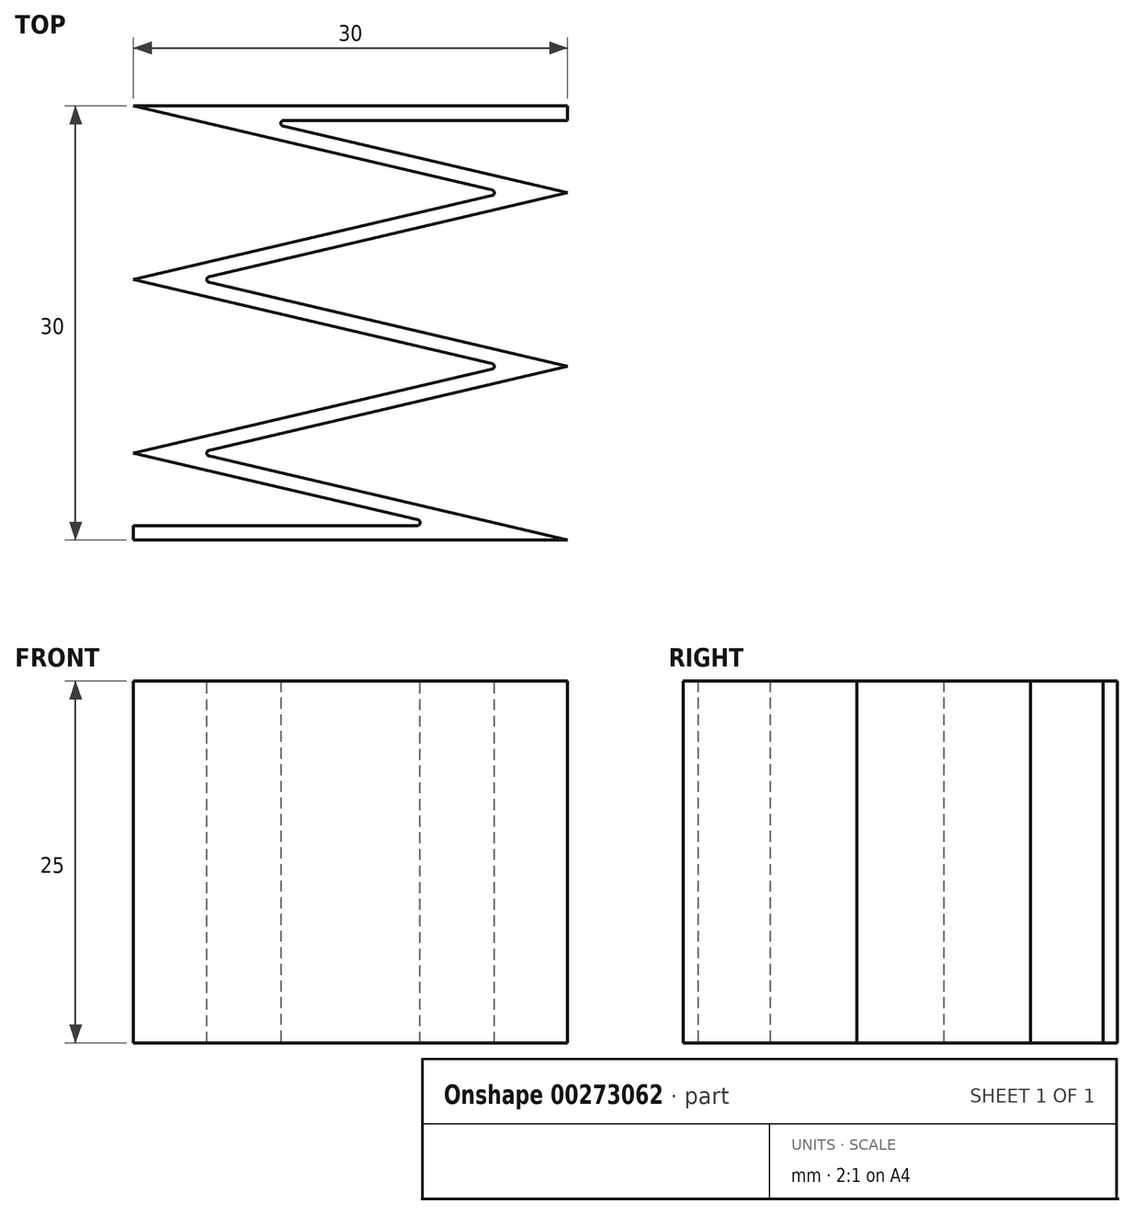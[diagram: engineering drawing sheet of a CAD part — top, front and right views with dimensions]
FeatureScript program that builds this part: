
annotation { "Feature Type Name" : "Feature", "Feature Type Description" : "" }
export const myFeature = defineFeature(function(context is Context, id is Id, definition is map)
    precondition{}
    {
        {
            var Q0;
            Q0=qCreatedBy(makeId("Top.planeOp"),FACE);
            var sketch = newSketch(context, id + "F0", { "sketchPlane" : qUnion([Q0])});
            skLineSegment(sketch, "E0", {"start": v(-25.67, 29.5) * mm, "end": v(-2.2, 24) * mm, "construction": true});
            skLineSegment(sketch, "E1", {"start": v(-2.2, 24) * mm, "end": v(-27.8, 18) * mm, "construction": true});
            skLineSegment(sketch, "E2", {"start": v(-27.8, 18) * mm, "end": v(-2.2, 12) * mm, "construction": true});
            skLineSegment(sketch, "E3", {"start": v(-2.2, 12) * mm, "end": v(-27.8, 6) * mm, "construction": true});
            skLineSegment(sketch, "E4", {"start": v(-27.8, 6) * mm, "end": v(-4.33, 0.5) * mm, "construction": true});
            skLineSegment(sketch, "E5", {"start": v(-4.33, 0.5) * mm, "end": v(-30, 0.5) * mm, "construction": true});
            skLineSegment(sketch, "E6", {"start": v(-25.67, 29.5) * mm, "end": v(0, 29.5) * mm, "construction": true});
            skLineSegment(sketch, "E7.0", {"start": v(-8.65, 1) * mm, "end": v(-30, 1) * mm});
            skLineSegment(sketch, "E7.1", {"start": v(-30, 6) * mm, "end": v(-8.65, 1) * mm});
            skLineSegment(sketch, "E7.2", {"start": v(-4.38, 12) * mm, "end": v(-30, 6) * mm});
            skLineSegment(sketch, "E7.3", {"start": v(-30, 30) * mm, "end": v(0, 30) * mm});
            skLineSegment(sketch, "E7.4", {"start": v(-30, 30) * mm, "end": v(-4.38, 24) * mm});
            skLineSegment(sketch, "E7.5", {"start": v(-4.38, 24) * mm, "end": v(-30, 18) * mm});
            skLineSegment(sketch, "E7.6", {"start": v(-30, 18) * mm, "end": v(-4.38, 12) * mm});
            skLineSegment(sketch, "E8.0", {"start": v(-21.35, 29) * mm, "end": v(0, 29) * mm});
            skLineSegment(sketch, "E8.1", {"start": v(-21.35, 29) * mm, "end": v(0, 24) * mm});
            skLineSegment(sketch, "E8.2", {"start": v(0, 24) * mm, "end": v(-25.62, 18) * mm});
            skLineSegment(sketch, "E8.3", {"start": v(0, 0) * mm, "end": v(-30, 0) * mm});
            skLineSegment(sketch, "E8.4", {"start": v(-25.62, 6) * mm, "end": v(0, 0) * mm});
            skLineSegment(sketch, "E8.5", {"start": v(0, 12) * mm, "end": v(-25.62, 6) * mm});
            skLineSegment(sketch, "E8.6", {"start": v(-25.62, 18) * mm, "end": v(0, 12) * mm});
            skLineSegment(sketch, "E9", {"start": v(0, 30) * mm, "end": v(0, 29) * mm});
            skLineSegment(sketch, "E10", {"start": v(-30, 1) * mm, "end": v(-30, 0) * mm});
            skLineSegment(sketch, "E11", {"start": v(-30, 30) * mm, "end": v(-30, 18) * mm, "construction": true});
            skPoint(sketch, "E12", {"position": v(-30, 24) * mm});
            skSolve(sketch);
        }
        {
            var Q0;
            Q0 = qSketchRegion(id + "F0", true);
            extrude(context, id + "F1", {"entities" : qUnion([Q0]), "depth" : 25 * mm});
        }
        {
            var Q0;
            Q0=makeQuery(id+"F1.opExtrude","SWEPT_EDGE",EDGE,{"disambiguationData":[OSD([sQuery(id+"F0.wireOp",EDGE,"E8.0"),sQuery(id+"F0.wireOp",EDGE,"E8.1")])]});
            var Q1;
            Q1=makeQuery(id+"F1.opExtrude","SWEPT_EDGE",EDGE,{"disambiguationData":[OSD([sQuery(id+"F0.wireOp",EDGE,"E8.2"),sQuery(id+"F0.wireOp",EDGE,"E8.6")])]});
            var Q2;
            Q2=makeQuery(id+"F1.opExtrude","SWEPT_EDGE",EDGE,{"disambiguationData":[OSD([sQuery(id+"F0.wireOp",EDGE,"E8.4"),sQuery(id+"F0.wireOp",EDGE,"E8.5")])]});
            var Q3;
            Q3=makeQuery(id+"F1.opExtrude","SWEPT_EDGE",EDGE,{"disambiguationData":[OSD([sQuery(id+"F0.wireOp",EDGE,"E7.0"),sQuery(id+"F0.wireOp",EDGE,"E7.1")])]});
            var Q4;
            Q4=makeQuery(id+"F1.opExtrude","SWEPT_EDGE",EDGE,{"disambiguationData":[OSD([sQuery(id+"F0.wireOp",EDGE,"E7.2"),sQuery(id+"F0.wireOp",EDGE,"E7.6")])]});
            var Q5;
            Q5=makeQuery(id+"F1.opExtrude","SWEPT_EDGE",EDGE,{"disambiguationData":[OSD([sQuery(id+"F0.wireOp",EDGE,"E7.4"),sQuery(id+"F0.wireOp",EDGE,"E7.5")])]});
            fillet(context, id + "F2", {"entities" : qUnion([Q0, Q1, Q2, Q3, Q4, Q5]), "radius" : 0.2 * mm, "tangentPropagation" : true, "allowEdgeOverflow" : false});
        }
    });
